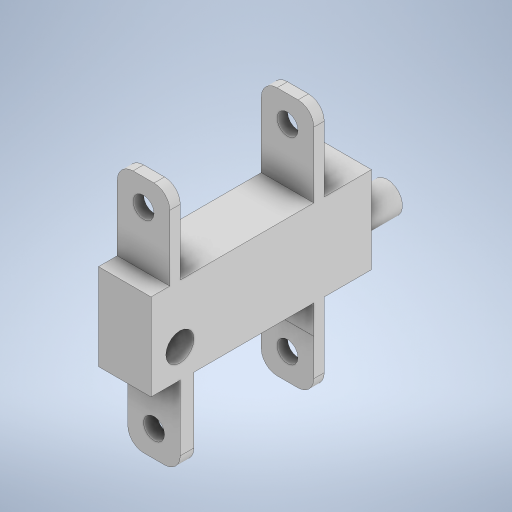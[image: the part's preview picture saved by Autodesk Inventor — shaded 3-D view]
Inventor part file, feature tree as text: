
AUTODESK INVENTOR PART (.ipt)
format: ipt  version: 2024 (Build 280153000, 153)  size: 356,864 bytes
history: native  units: in
note: dims shown in document units (in); Inventor stores cm internally (conversion verified against a paired STEP export)
features: extrude x13, sketch x13, fillet x4
ambient origin geometry x8: Origin, YZ Plane, XZ Plane, XY Plane, X Axis, Y Axis, Z Axis, Center Point
bodies: Solid1 (feature_tree)
feature tree (30):
  extrude  "Extrusion1"  Depth=0.3937in
  extrude  "Extrusion3"  Depth=0.8661in
  extrude  "Extrusion4"  Depth=0.315in TaperAngle=0.0deg
  fillet  "Fillet1"  Radius=0.2362in
  extrude  "Extrusion5"  Depth=0.3937in TaperAngle=0.0deg
  extrude  "Extrusion6"  Depth=0.1181in
  extrude  "Extrusion7"  Depth=0.1575in
  extrude  "Extrusion8"  Depth=0.2165in TaperAngle=0.0deg
  extrude  "Extrusion9"  Depth=0.4331in
  fillet  "Fillet3"  Radius=0.4331in
  extrude  "Extrusion10"  Depth=1.5748in TaperAngle=0.0deg
  extrude  "Extrusion11"  Depth=0.6102in TaperAngle=0.0deg
  fillet  "Fillet4"  Radius=0.1181in
  extrude  "Extrusion12"  Depth=0.1575in
  extrude  "Extrusion13"  Depth=0.6102in TaperAngle=0.0deg
  fillet  "Fillet5"  Radius=0.1181in
  extrude  "Extrusion14"  Depth=0.6102in TaperAngle=0.0deg
  sketch  "Sketch1"  dims[d0=0.5906in d1=0.3937in]
  sketch  "Sketch3"  dims[d2=0.8661in d3=0.0in d9=0.1969in]
  sketch  "Sketch4"  dims[d10=0.2283in d11=0.315in d12=0.0in d13=0.2362in]
  sketch  "Sketch5"  dims[d14=0.0787in d15=0.3937in d16=0.0in]
  sketch  "Sketch6"  dims[d17=0.1181in d18=0.1969in]
  sketch  "Sketch7"  dims[d19=0.1969in d20=0.1575in]
  sketch  "Sketch8"  dims[d21=0.3937in d22=0.0in d24=0.2165in d25=0.0in]
  sketch  "Sketch9"  dims[d26=1.063in d27=0.0in d28=1.437in d29=0.4331in]
  sketch  "Sketch10"  dims[d30=0.2106in d31=1.5748in d32=0.0in]
  sketch  "Sketch11"  dims[d33=0.0787in d34=0.6102in d35=0.0in d36=0.1181in]
  sketch  "Sketch12"  dims[d37=0.1969in d38=0.1575in]
  sketch  "Sketch13"  dims[d39=0.6102in d40=0.0in d41=0.6102in d42=0.0in d43=0.1181in]
  sketch  "Sketch14"  dims[d44=0.3937in d45=0.0in d46=0.6102in d47=0.0in d48=0.1181in d49=0.6102in d50=0.0in]
